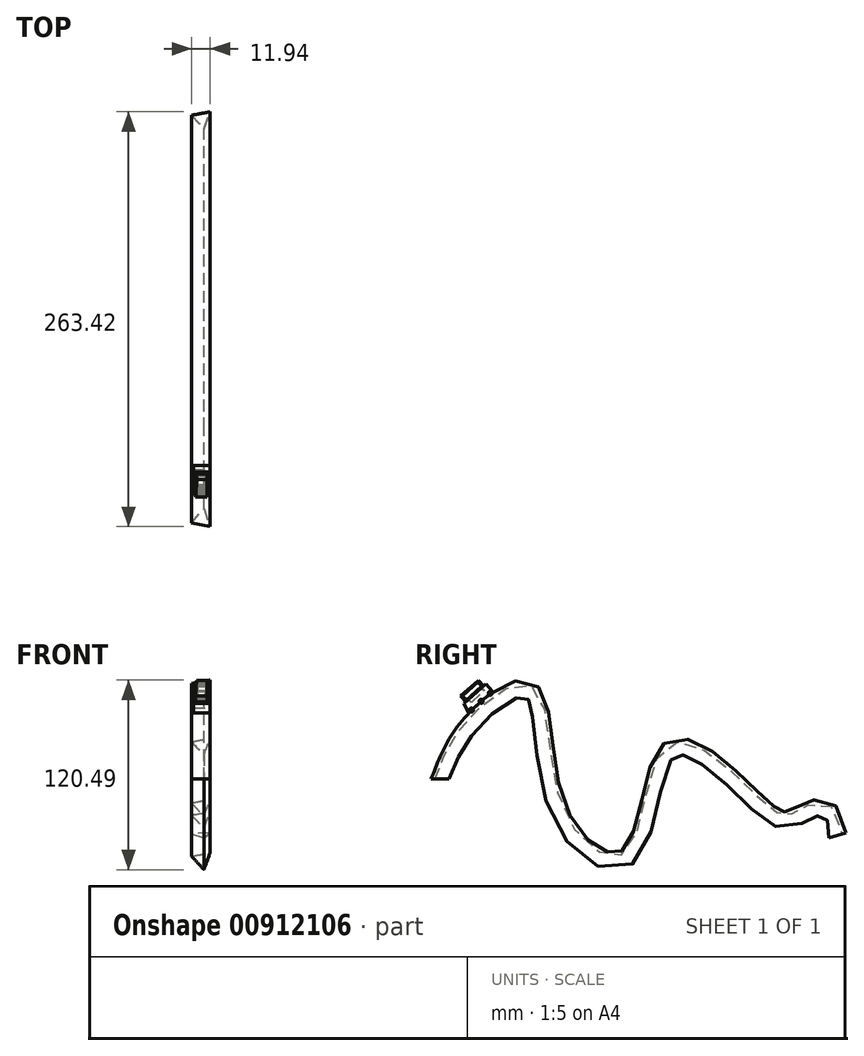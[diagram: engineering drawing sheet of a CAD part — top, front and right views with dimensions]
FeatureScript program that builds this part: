
annotation { "Feature Type Name" : "Feature", "Feature Type Description" : "" }
export const myFeature = defineFeature(function(context is Context, id is Id, definition is map)
    precondition{}
    {
        {
            var Q0;
            Q0=qCreatedBy(makeId("Right.planeOp"),FACE);
            var sketch = newSketch(context, id + "F0", { "sketchPlane" : qUnion([Q0])});
            skFitSpline(sketch, "E0", {"points": [v(-73.2, 0) * mm, v(-53.2, 36.25) * mm, v(-14.86, 57.37) * mm, v(4.58, -20.97) * mm, v(46.81, -48.2) * mm, v(71.26, 17.92) * mm, v(107.93, 6.8) * mm, v(146.82, -24.86) * mm, v(164.6, -17.64) * mm, v(181.27, -35.42) * mm], "startDerivative": vector(126.14, 332.23) * mm, "endDerivative": vector(-40.6, -568.28) * mm});
            skSolve(sketch);
        }
        {
            var Q0;
            Q0=qCreatedBy(makeId("Top.planeOp"),FACE);
            var sketch = newSketch(context, id + "F1", { "sketchPlane" : qUnion([Q0])});
            skCircle(sketch, "E1.cCircle", {"center": v(0, -73.2) * mm, "radius": 3.47 * mm, "construction": true});
            skLineSegment(sketch, "E1.0", {"start": v(1.34, -66.4) * mm, "end": v(5.22, -77.76) * mm});
            skLineSegment(sketch, "E1.1", {"start": v(5.22, -77.76) * mm, "end": v(-6.56, -75.45) * mm});
            skLineSegment(sketch, "E1.2", {"start": v(-6.56, -75.45) * mm, "end": v(1.34, -66.4) * mm});
            skPoint(sketch, "E1.0.midPoint", {"position": v(3.28, -72.08) * mm});
            skSolve(sketch);
        }
        {
            var Q0;
            Q0=makeQuery(id+"F1.imprint","IMPRINT",FACE,{"disambiguationData":[TD([[makeQuery(id+"F1.imprint","IMPRINT",EDGE,{"derivedFrom":sQuery(id+"F1.wireOp",EDGE,"E1.0")}),-1.0]])]});
            var Q1;
            Q1=sQuery(id+"F0.wireOp",EDGE,"E0");
            sweep(context, id + "F2", {"profiles" : qUnion([Q0]), "path" : qUnion([Q1])});
        }
        {
            var Q0;
            Q0=qCreatedBy(makeId("Right.planeOp"),FACE);
            var sketch = newSketch(context, id + "F3", { "sketchPlane" : qUnion([Q0])});
            skLineSegment(sketch, "E2", {"start": v(-57.03, 47.97) * mm, "end": v(-54.23, 42.1) * mm});
            skLineSegment(sketch, "E3", {"start": v(-54.23, 42.1) * mm, "end": v(-38.9, 55.75) * mm});
            skLineSegment(sketch, "E4", {"start": v(-38.9, 55.75) * mm, "end": v(-43.06, 60.42) * mm});
            skLineSegment(sketch, "E5", {"start": v(-43.06, 60.42) * mm, "end": v(-57.03, 47.97) * mm});
            skSolve(sketch);
        }
        {
            var Q0;
            Q0=makeQuery(id+"F3.imprint","IMPRINT",FACE,{"disambiguationData":[TD([[makeQuery(id+"F3.imprint","IMPRINT",EDGE,{"derivedFrom":sQuery(id+"F3.wireOp",EDGE,"E2")}),1.0]])]});
            extrude(context, id + "F4", {"entities" : qUnion([Q0]), "endBound" : BoundingType.SYMMETRIC, "depth" : 10.77 * mm, "offsetDistance" : 25.4 * mm});
        }
        {
            var Q0;
            Q0=makeQuery(id+"F4.opExtrude","CAP_FACE",FACE,{"disambiguationData":[OSD([sQuery(id+"F3.wireOp",EDGE,"E2"),sQuery(id+"F3.wireOp",EDGE,"E3"),sQuery(id+"F3.wireOp",EDGE,"E4"),sQuery(id+"F3.wireOp",EDGE,"E5")])],"isStart":false});
            var sketch = newSketch(context, id + "F5", { "sketchPlane" : qUnion([Q0])});
            skCircle(sketch, "E6", {"center": v(-52.27, 43.83) * mm, "radius": 1.27 * mm});
            skCircle(sketch, "E7", {"center": v(-45.98, 49.44) * mm, "radius": 1.27 * mm});
            skCircle(sketch, "E8", {"center": v(-40.25, 54.55) * mm, "radius": 1.27 * mm});
            skPoint(sketch, "E9", {"position": v(-55.63, 45.03) * mm});
            skSolve(sketch);
        }
        {
            var Q0;
            {var subQ0=sQuery(id+"F5.wireOp",EDGE,"E6");var subQ1=makeQuery(id+"F4.opExtrude","CAP_EDGE",EDGE,{"disambiguationData":[OSD([sQuery(id+"F3.wireOp",EDGE,"E3")])],"isStart":false});var subQ2=makeQuery(id+"F5.imprint","INTERSECT",VERTEX,{"disambiguationData":[OD(0.0)],"derivedFrom":[subQ1,subQ0]});Q0=makeQuery(id+"F5.imprint","IMPRINT",FACE,{"disambiguationData":[TD([[makeQuery(id+"F5.imprint","IMPRINT",EDGE,{"disambiguationData":[TD([[subQ2,1.0]])],"derivedFrom":subQ0}),1.0]])]});}
            var Q1;
            {var subQ0=sQuery(id+"F5.wireOp",EDGE,"E6");var subQ1=makeQuery(id+"F4.opExtrude","CAP_EDGE",EDGE,{"disambiguationData":[OSD([sQuery(id+"F3.wireOp",EDGE,"E3")])],"isStart":false});var subQ2=makeQuery(id+"F5.imprint","INTERSECT",VERTEX,{"disambiguationData":[OD(0.0)],"derivedFrom":[subQ1,subQ0]});Q1=makeQuery(id+"F5.imprint","IMPRINT",FACE,{"disambiguationData":[TD([[makeQuery(id+"F5.imprint","IMPRINT",EDGE,{"disambiguationData":[TD([[subQ2,-1.0]])],"derivedFrom":subQ0}),1.0]])]});}
            var Q2;
            {var subQ0=sQuery(id+"F5.wireOp",EDGE,"E7");var subQ1=makeQuery(id+"F4.opExtrude","CAP_EDGE",EDGE,{"disambiguationData":[OSD([sQuery(id+"F3.wireOp",EDGE,"E3")])],"isStart":false});var subQ2=makeQuery(id+"F5.imprint","INTERSECT",VERTEX,{"disambiguationData":[OD(0.0)],"derivedFrom":[subQ1,subQ0]});Q2=makeQuery(id+"F5.imprint","IMPRINT",FACE,{"disambiguationData":[TD([[makeQuery(id+"F5.imprint","IMPRINT",EDGE,{"disambiguationData":[TD([[subQ2,1.0]])],"derivedFrom":subQ0}),1.0]])]});}
            var Q3;
            {var subQ0=sQuery(id+"F5.wireOp",EDGE,"E7");var subQ1=makeQuery(id+"F4.opExtrude","CAP_EDGE",EDGE,{"disambiguationData":[OSD([sQuery(id+"F3.wireOp",EDGE,"E3")])],"isStart":false});var subQ2=makeQuery(id+"F5.imprint","INTERSECT",VERTEX,{"disambiguationData":[OD(0.0)],"derivedFrom":[subQ1,subQ0]});Q3=makeQuery(id+"F5.imprint","IMPRINT",FACE,{"disambiguationData":[TD([[makeQuery(id+"F5.imprint","IMPRINT",EDGE,{"disambiguationData":[TD([[subQ2,-1.0]])],"derivedFrom":subQ0}),1.0]])]});}
            var Q4;
            {var subQ0=sQuery(id+"F5.wireOp",EDGE,"E8");var subQ1=makeQuery(id+"F4.opExtrude","CAP_EDGE",EDGE,{"disambiguationData":[OSD([sQuery(id+"F3.wireOp",EDGE,"E3")])],"isStart":false});var subQ2=makeQuery(id+"F5.imprint","INTERSECT",VERTEX,{"disambiguationData":[OD(0.0)],"derivedFrom":[subQ1,subQ0]});Q4=makeQuery(id+"F5.imprint","IMPRINT",FACE,{"disambiguationData":[TD([[makeQuery(id+"F5.imprint","IMPRINT",EDGE,{"disambiguationData":[TD([[subQ2,-1.0]])],"derivedFrom":subQ0}),1.0]])]});}
            var Q5;
            {var subQ0=sQuery(id+"F5.wireOp",EDGE,"E8");var subQ1=makeQuery(id+"F4.opExtrude","CAP_EDGE",EDGE,{"disambiguationData":[OSD([sQuery(id+"F3.wireOp",EDGE,"E3")])],"isStart":false});var subQ2=makeQuery(id+"F5.imprint","INTERSECT",VERTEX,{"disambiguationData":[OD(0.0)],"derivedFrom":[subQ1,subQ0]});Q5=makeQuery(id+"F5.imprint","IMPRINT",FACE,{"disambiguationData":[TD([[makeQuery(id+"F5.imprint","IMPRINT",EDGE,{"disambiguationData":[TD([[subQ2,1.0]])],"derivedFrom":subQ0}),1.0]])]});}
            extrude(context, id + "F6", {"entities" : qUnion([Q0, Q1, Q2, Q3, Q4, Q5]), "oppositeDirection" : true, "depth" : 11.18 * mm, "offsetDistance" : 25.4 * mm});
        }
        {
            var Q0;
            Q0=makeQuery(id+"F4.opExtrude","SWEPT_FACE",FACE,{"disambiguationData":[OSD([sQuery(id+"F3.wireOp",EDGE,"E5")])]});
            var sketch = newSketch(context, id + "F7", { "sketchPlane" : qUnion([Q0])});
            skLineSegment(sketch, "E10", {"start": v(-3.83, -9.03) * mm, "end": v(3.4, -9.03) * mm});
            skLineSegment(sketch, "E11", {"start": v(3.4, -9.03) * mm, "end": v(3.4, 6.12) * mm});
            skLineSegment(sketch, "E12", {"start": v(3.4, 6.12) * mm, "end": v(-3.48, 6.12) * mm});
            skLineSegment(sketch, "E13", {"start": v(-3.48, 6.12) * mm, "end": v(-3.83, -9.03) * mm});
            skSolve(sketch);
        }
        {
            var Q0;
            Q0=makeQuery(id+"F7.imprint","IMPRINT",FACE,{"disambiguationData":[TD([[makeQuery(id+"F7.imprint","IMPRINT",EDGE,{"derivedFrom":sQuery(id+"F7.wireOp",EDGE,"E10")}),1.0]])]});
            extrude(context, id + "F8", {"entities" : qUnion([Q0]), "operationType" : NewBodyOperationType.REMOVE, "oppositeDirection" : true, "depth" : 3.43 * mm, "offsetDistance" : 25.4 * mm});
        }
        {
            var Q0;
            Q0=makeQuery(id+"F8.boolean.opBoolean","COPY",FACE,{"derivedFrom":makeQuery(id+"F8.opExtrude","CAP_FACE",FACE,{"disambiguationData":[OSD([sQuery(id+"F7.wireOp",EDGE,"E10"),sQuery(id+"F7.wireOp",EDGE,"E11"),sQuery(id+"F7.wireOp",EDGE,"E12"),sQuery(id+"F7.wireOp",EDGE,"E13")])],"isStart":false})});
            extrude(context, id + "F9", {"entities" : qUnion([Q0]), "operationType" : NewBodyOperationType.ADD, "depth" : 8.38 * mm, "offsetDistance" : 25.4 * mm});
        }
        {
            var Q0;
            Q0=makeQuery(id+"F9.opExtrude","SWEPT_FACE",FACE,{"disambiguationData":[OSD([sQuery(id+"F7.wireOp",EDGE,"E13")])]});
            var sketch = newSketch(context, id + "F10", { "sketchPlane" : qUnion([Q0])});
            skLineSegment(sketch, "E14", {"start": v(48, 61.64) * mm, "end": v(45.66, 59.05) * mm});
            skLineSegment(sketch, "E15", {"start": v(45.66, 59.05) * mm, "end": v(55.6, 50.19) * mm});
            skLineSegment(sketch, "E16", {"start": v(57.79, 52.87) * mm, "end": v(55.6, 50.19) * mm});
            skLineSegment(sketch, "E17", {"start": v(48, 61.64) * mm, "end": v(57.79, 52.87) * mm});
            skSolve(sketch);
        }
        {
            var Q0;
            Q0=makeQuery(id+"F10.imprint","IMPRINT",FACE,{"disambiguationData":[TD([[makeQuery(id+"F10.imprint","IMPRINT",EDGE,{"derivedFrom":sQuery(id+"F10.wireOp",EDGE,"E14")}),1.0]])]});
            extrude(context, id + "F11", {"entities" : qUnion([Q0]), "operationType" : NewBodyOperationType.REMOVE, "endBound" : BoundingType.THROUGH_ALL, "oppositeDirection" : true, "depth" : 25.4 * mm, "offsetDistance" : 25.4 * mm});
        }
        {
            var Q0;
            Q0=makeQuery(id+"F11.boolean.opBoolean","COPY",FACE,{"derivedFrom":makeQuery(id+"F11.opExtrude","SWEPT_FACE",FACE,{"disambiguationData":[OSD([sQuery(id+"F10.wireOp",EDGE,"E15")])]})});
            var sketch = newSketch(context, id + "F12", { "sketchPlane" : qUnion([Q0])});
            skLineSegment(sketch, "E18", {"start": v(2.67, 4.56) * mm, "end": v(-2.34, 4.68) * mm});
            skLineSegment(sketch, "E19", {"start": v(-2.34, -6.58) * mm, "end": v(-2.34, 4.68) * mm});
            skLineSegment(sketch, "E20", {"start": v(-2.34, -6.58) * mm, "end": v(2.22, -6.58) * mm});
            skLineSegment(sketch, "E21", {"start": v(2.22, -6.58) * mm, "end": v(2.67, 4.56) * mm});
            skSolve(sketch);
        }
        {
            var Q0;
            Q0=makeQuery(id+"F12.imprint","IMPRINT",FACE,{"disambiguationData":[TD([[makeQuery(id+"F12.imprint","IMPRINT",EDGE,{"derivedFrom":sQuery(id+"F12.wireOp",EDGE,"E18")}),1.0]])]});
            extrude(context, id + "F13", {"entities" : qUnion([Q0]), "operationType" : NewBodyOperationType.REMOVE, "oppositeDirection" : true, "depth" : 3.3 * mm, "offsetDistance" : 25.4 * mm});
        }
    });
